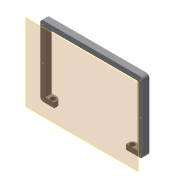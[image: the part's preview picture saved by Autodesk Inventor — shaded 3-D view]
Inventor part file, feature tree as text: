
AUTODESK INVENTOR PART (.ipt)
format: ipt  version: 2019.4 (Build 234330000, 330)  size: 232,960 bytes
history: native  units: mm
features: sketch x7, extrude x6, projected_geometry x4, other x3, plane x2, fillet x2, reference x2, hole x1, pattern_linear x1
ambient origin geometry x8: Origin, YZ Plane, XZ Plane, XY Plane, X Axis, Y Axis, Z Axis, Center Point
bodies: Solid1 (feature_tree)
feature tree (28):
  plane  "Work Plane1"
  extrude  "Extrusion1"  Depth=6.0mm TaperAngle=0.0deg
  sketch  "Sketch2"  dims[d5=10.0mm d6=0.0mm d8=8.0mm]
  plane  "Work Plane2"
  extrude  "Extrusion2"  Depth=8.0mm
  extrude  "Extrusion3"  Depth=6.0mm
  fillet  "Fillet1"  Radius=6.0mm
  fillet  "Fillet2"  Radius=120.0mm
  hole  "Hole1"  [1 undecoded]
  extrude  "Extrusion4"  Depth=10.0mm
  pattern_linear  "Rectangular Pattern1"  Count1=5  [1 undecoded]
  extrude  "Extrusion5"  Depth=8.0mm
  extrude  "Extrusion6"  Depth=7.0mm TaperAngle=0.0deg
  sketch  "Sketch1"  dims[d0=5.0mm d1=0.0mm d3=6.0mm d4=0.0mm]
  reference  "Reference1"
  projected_geometry  "Projected Loop1"
  sketch  "Sketch3"  dims[d9=0.0mm d10=6.0mm d11=6.0mm]
  projected_geometry  "Projected Loop2"
  projected_geometry  "Projected Loop3"
  sketch  "Sketch4"  dims[d12=2.9mm d13=6.0mm d14=6.0mm d15=4.0mm d16=90.0deg d17=15.0mm d18=20.594885mm d19=120.0mm]
  projected_geometry  "Projected Loop4"
  reference  "Reference2"
  sketch  "Sketch5"  dims[d20=80.0mm d21=2.9mm]
  sketch  "Sketch6"  dims[d22=10.0mm d23=0.0mm d24=70.0mm d26=20.0mm d27=50.0mm d29=20.0mm]
  sketch  "Sketch7"  dims[d30=8.0mm d31=8.0mm d32=7.0mm d33=0.0mm d34=10.0mm d35=0.0mm]
  other  "<userpath>\Dropbox\cellSTORM\cellSTORM_v6.iam"
  other  "cellSTORM_v6.iam"
  other  "cellSTORM_Base_v0_R1:1"
note: 2 required parameter values undecoded (feature->parameter linkage not recoverable at this tier; creation-order binding heuristic only, values carry confidence <= 0.55)
